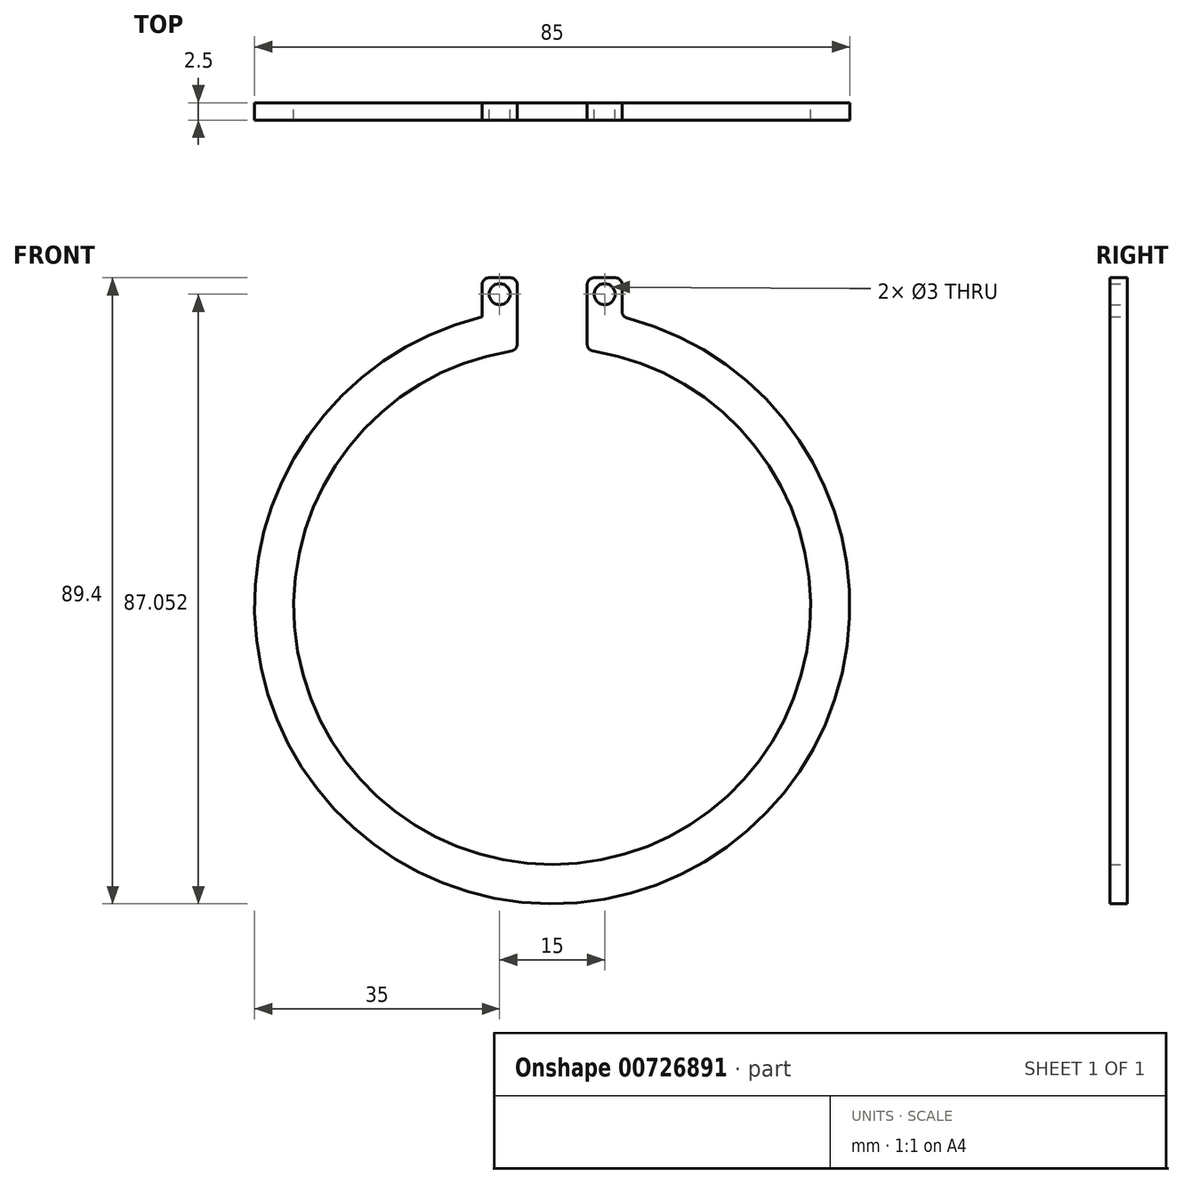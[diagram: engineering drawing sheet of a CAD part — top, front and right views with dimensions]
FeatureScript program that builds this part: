
annotation { "Feature Type Name" : "Feature", "Feature Type Description" : "" }
export const myFeature = defineFeature(function(context is Context, id is Id, definition is map)
    precondition{}
    {
        {
            var Q0;
            Q0=qCreatedBy(makeId("Front.planeOp"),FACE);
            var sketch = newSketch(context, id + "F0", { "sketchPlane" : qUnion([Q0])});
            skArc(sketch, "E0", {"start": v(-5, 36.56) * mm, "mid": v(0, -36.9) * mm, "end": v(5, 36.56) * mm});
            skArc(sketch, "E1", {"start": v(-10, 41.3) * mm, "mid": v(0, -42.5) * mm, "end": v(10, 41.3) * mm});
            skLineSegment(sketch, "E2", {"start": v(-10, 41.3) * mm, "end": v(-10, 46.9) * mm});
            skLineSegment(sketch, "E3", {"start": v(-10, 46.9) * mm, "end": v(-10, 41.3) * mm});
            skLineSegment(sketch, "E4", {"start": v(10, 41.3) * mm, "end": v(10, 46.9) * mm});
            skLineSegment(sketch, "E5", {"start": v(10, 46.9) * mm, "end": v(5, 46.9) * mm});
            skLineSegment(sketch, "E6", {"start": v(5, 46.9) * mm, "end": v(5, 42.2) * mm});
            skLineSegment(sketch, "E7", {"start": v(-10, 46.9) * mm, "end": v(-5, 46.9) * mm});
            skLineSegment(sketch, "E8", {"start": v(-5, 46.9) * mm, "end": v(-5, 42.2) * mm});
            skLineSegment(sketch, "E9", {"start": v(-5, 42.2) * mm, "end": v(-5, 36.9) * mm});
            skLineSegment(sketch, "E10", {"start": v(5, 42.2) * mm, "end": v(5, 36.9) * mm});
            skLineSegment(sketch, "E11", {"start": v(-5, 36.9) * mm, "end": v(-5, 36.56) * mm});
            skLineSegment(sketch, "E12", {"start": v(5, 36.9) * mm, "end": v(5, 36.56) * mm});
            skPoint(sketch, "E13.end.orphan", {"position": v(10, 36.9) * mm});
            skLineSegment(sketch, "E14", {"start": v(-5, 46.9) * mm, "end": v(-7.5, 46.9) * mm});
            skLineSegment(sketch, "E15", {"start": v(10, 46.9) * mm, "end": v(7.5, 46.9) * mm});
            skCircle(sketch, "E16", {"center": v(-7.5, 44.55) * mm, "radius": 1.5 * mm});
            skCircle(sketch, "E17", {"center": v(7.5, 44.55) * mm, "radius": 1.5 * mm});
            skPoint(sketch, "E18.trimOffspring.end.orphan", {"position": v(-7.5, 42.2) * mm});
            skPoint(sketch, "E19.start.orphan", {"position": v(7.5, 42.2) * mm});
            skPoint(sketch, "E20.end.orphan", {"position": v(0, 36.9) * mm});
            skSolve(sketch);
        }
        {
            var Q0;
            Q0 = qSketchRegion(id + "F0", true);
            extrude(context, id + "F1", {"entities" : qUnion([Q0]), "depth" : 2.5 * mm, "offsetDistance" : 25 * mm});
        }
        {
            var Q0;
            Q0=makeQuery(id+"F1.opExtrude","SWEPT_EDGE",EDGE,{"disambiguationData":[OSD([sQuery(id+"F0.wireOp",EDGE,"E3"),sQuery(id+"F0.wireOp",EDGE,"E7")])]});
            var Q1;
            Q1=makeQuery(id+"F1.opExtrude","SWEPT_EDGE",EDGE,{"disambiguationData":[OSD([sQuery(id+"F0.wireOp",EDGE,"E8"),sQuery(id+"F0.wireOp",EDGE,"E14")])]});
            var Q2;
            Q2=makeQuery(id+"F1.opExtrude","SWEPT_EDGE",EDGE,{"disambiguationData":[OSD([sQuery(id+"F0.wireOp",EDGE,"E5"),sQuery(id+"F0.wireOp",EDGE,"E6")])]});
            var Q3;
            Q3=makeQuery(id+"F1.opExtrude","SWEPT_EDGE",EDGE,{"disambiguationData":[OSD([sQuery(id+"F0.wireOp",EDGE,"E4"),sQuery(id+"F0.wireOp",EDGE,"E15")])]});
            var Q4;
            Q4=makeQuery(id+"F1.opExtrude","SWEPT_EDGE",EDGE,{"disambiguationData":[OSD([sQuery(id+"F0.wireOp",EDGE,"E0"),sQuery(id+"F0.wireOp",EDGE,"E12")])]});
            var Q5;
            Q5=makeQuery(id+"F1.opExtrude","SWEPT_EDGE",EDGE,{"disambiguationData":[OSD([sQuery(id+"F0.wireOp",EDGE,"E0"),sQuery(id+"F0.wireOp",EDGE,"E11")])]});
            fillet(context, id + "F2", {"entities" : qUnion([Q0, Q1, Q2, Q3, Q4, Q5]), "radius" : 1 * mm, "tangentPropagation" : true, "allowEdgeOverflow" : false});
        }
    });
